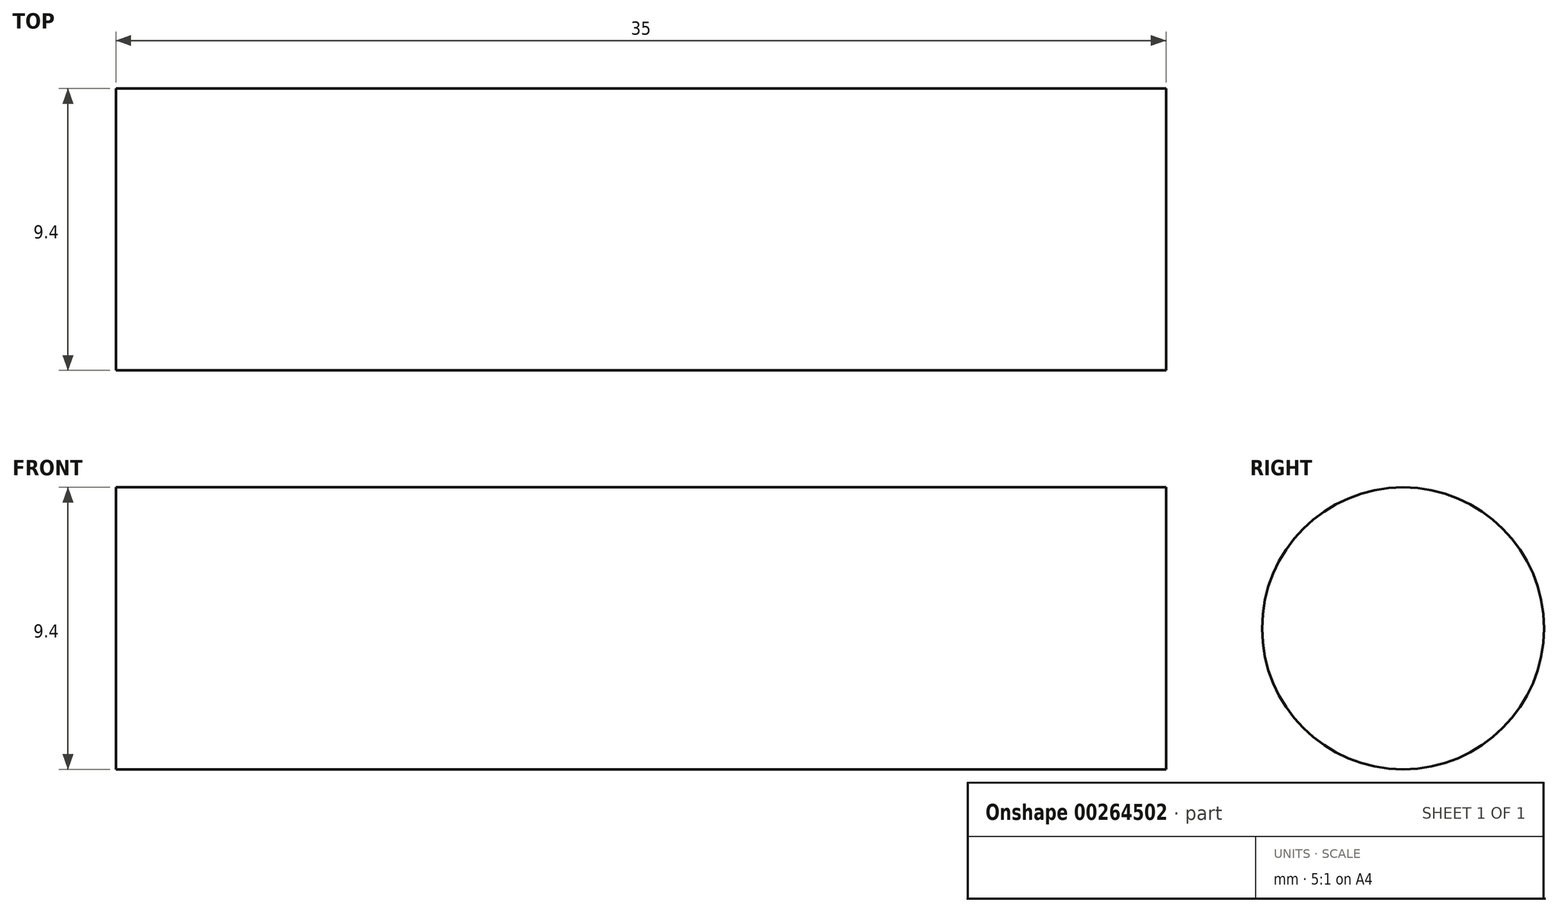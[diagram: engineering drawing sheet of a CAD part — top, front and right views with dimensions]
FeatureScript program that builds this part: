
annotation { "Feature Type Name" : "Feature", "Feature Type Description" : "" }
export const myFeature = defineFeature(function(context is Context, id is Id, definition is map)
    precondition{}
    {
        {
            var Q0;
            Q0=qCreatedBy(makeId("Right.planeOp"),FACE);
            var sketch = newSketch(context, id + "F0", { "sketchPlane" : qUnion([Q0])});
            skCircle(sketch, "E0", {"center": v(0, 0) * mm, "radius": 4.7 * mm});
            skSolve(sketch);
        }
        {
            var Q0;
            Q0 = qSketchRegion(id + "F0", true);
            extrude(context, id + "F1", {"entities" : qUnion([Q0]), "depth" : 17.5 * mm, "hasSecondDirection" : true, "secondDirectionOppositeDirection" : true, "secondDirectionDepth" : 17.5 * mm});
        }
    });
